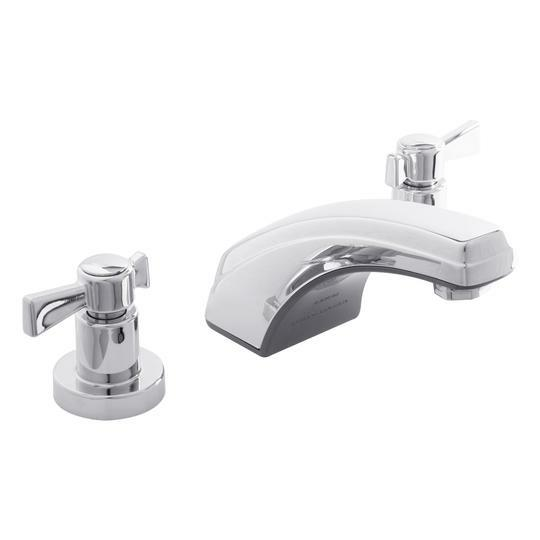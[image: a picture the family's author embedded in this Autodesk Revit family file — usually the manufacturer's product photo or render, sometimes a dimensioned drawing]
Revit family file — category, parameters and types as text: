
# Revit family: 01-1703-11  MEZCLADOR LAVAMANOS PLASTICO 8” HELIX PALA
name_source: partatom
category: Plumbing Fixtures
revit_build: Autodesk Revit 2018 (Build: 20170223_1515(x64)
units: mm (PartAtom-declared; Revit-internal decimal feet)

## family parameters
Cut with Voids When Loaded = No
Host = Face
OmniClass Number = 23.31.11.00
Part Type = Normal
Room Calculation Point = No
Round Connector Dimension = Use Diameter
Shared = No

## types (1)
- 01-1703-11
    Alto = 90.7 mm
    Alto - Aireador = 68.5 mm  [stored 0.224738 ft]
    Ancho manija = 67 mm
    CW Connection = Yes
    Default Elevation = 0 mm  [stored 0 ft]
    Description = Bimando baño
    Eje ( Rosca) = 203.2 mm  [stored 0.666667 ft]
    Eje-Aireador = 122.6 mm  [stored 0.402231 ft]
    HW Connection = Yes
    Link ficha tecnica = http://infotecnica.gricol.com
    Manufacturer = Gricol
    Model = 01-1703-11
    Plastico ABS Cromado = Plastico - ABS Cromado
    Product Name = MEZCLADOR LAVAMANOS PLASTICO 8” HELIX PALA
    Type Image = MEZCLADOR LAVAMANOS PLASTICO 8” HELIX PALA.jpg
    URL = https://www.gricol.com
    Vent Connection = No
    Waste Connection = No

note: [stored X ft] marks values corroborated as IEEE doubles in the binary element streams (Revit-internal decimal feet)

## geometry (parser evidence)
native form markers: Blend x4, Sweep x9
no freeform markers — native parametric forms only
